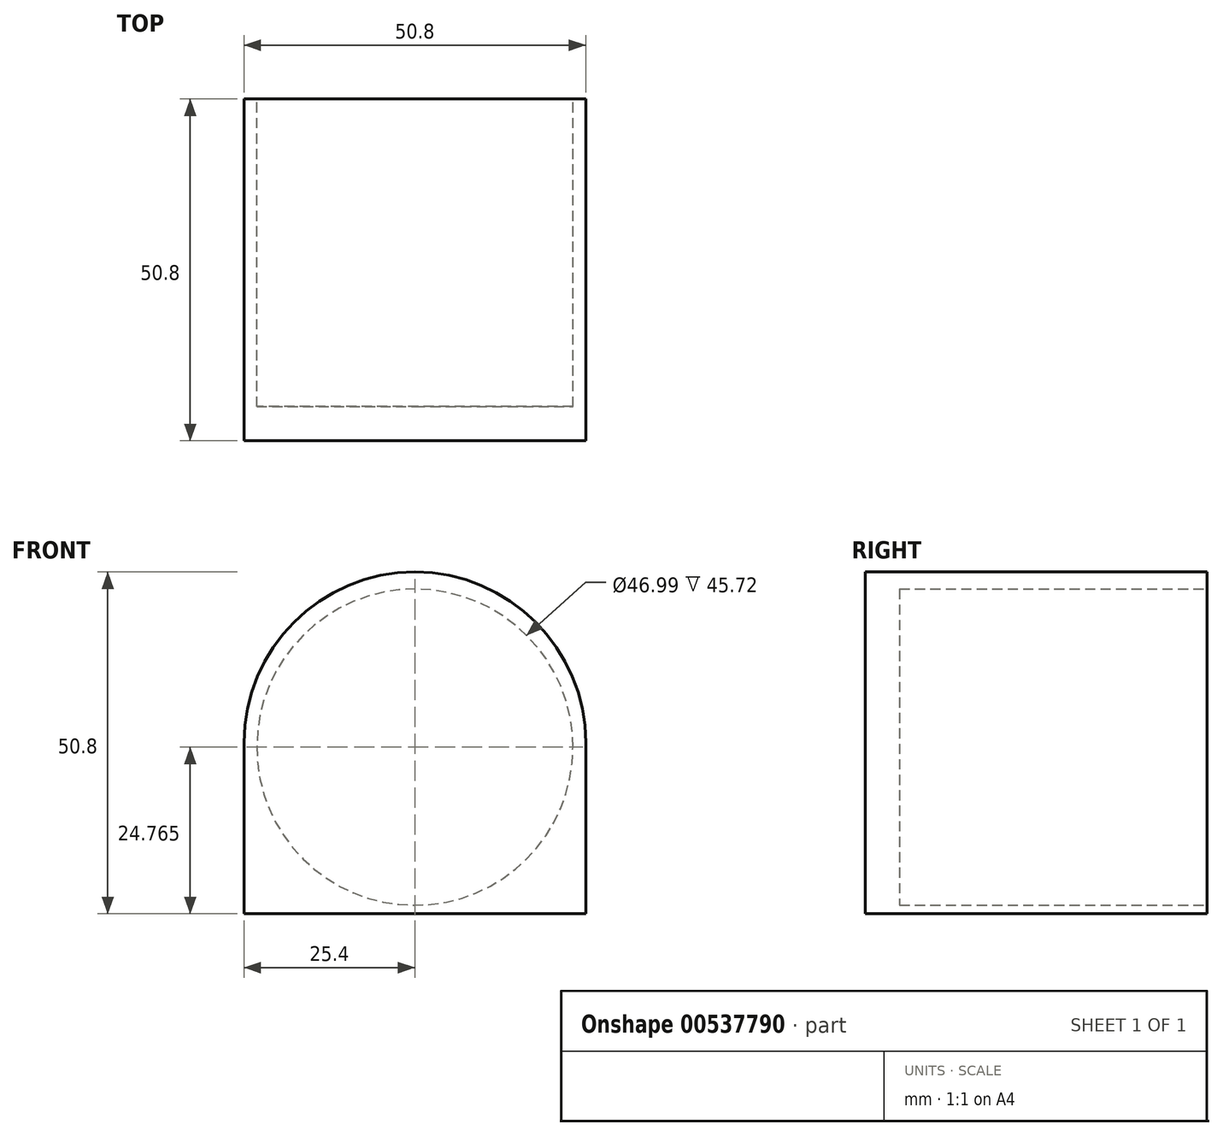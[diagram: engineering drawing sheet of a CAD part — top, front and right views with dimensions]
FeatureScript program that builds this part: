
annotation { "Feature Type Name" : "Feature", "Feature Type Description" : "" }
export const myFeature = defineFeature(function(context is Context, id is Id, definition is map)
    precondition{}
    {
        {
            var Q0;
            Q0=qCreatedBy(makeId("Top.planeOp"),FACE);
            var sketch = newSketch(context, id + "F0", { "sketchPlane" : qUnion([Q0])});
            skLineSegment(sketch, "E0", {"start": v(0, 0) * mm, "end": v(-50.8, 0) * mm});
            skLineSegment(sketch, "E1", {"start": v(-50.8, 0) * mm, "end": v(-50.8, 50.8) * mm});
            skLineSegment(sketch, "E2", {"start": v(-50.8, 50.8) * mm, "end": v(0, 50.8) * mm});
            skLineSegment(sketch, "E3", {"start": v(0, 50.8) * mm, "end": v(0, 0) * mm});
            skSolve(sketch);
        }
        {
            var Q0;
            Q0=makeQuery(id+"F0.imprint","IMPRINT",FACE,{"disambiguationData":[TD([[makeQuery(id+"F0.imprint","IMPRINT",EDGE,{"derivedFrom":sQuery(id+"F0.wireOp",EDGE,"E0")}),-1.0]])]});
            extrude(context, id + "F1", {"entities" : qUnion([Q0]), "depth" : 50.8 * mm, "offsetDistance" : 25.4 * mm});
        }
        {
            var Q0;
            Q0=makeQuery(id+"F1.opExtrude","SWEPT_FACE",FACE,{"disambiguationData":[OSD([sQuery(id+"F0.wireOp",EDGE,"E2")])]});
            var sketch = newSketch(context, id + "F2", { "sketchPlane" : qUnion([Q0])});
            skCircle(sketch, "E4", {"center": v(25.4, 24.77) * mm, "radius": 23.5 * mm});
            skSolve(sketch);
        }
        {
            var Q0;
            Q0=makeQuery(id+"F1.opExtrude","CAP_EDGE",EDGE,{"disambiguationData":[OSD([sQuery(id+"F0.wireOp",EDGE,"E3")])],"isStart":false});
            var Q1;
            Q1=makeQuery(id+"F1.opExtrude","CAP_EDGE",EDGE,{"disambiguationData":[OSD([sQuery(id+"F0.wireOp",EDGE,"E1")])],"isStart":false});
            fillet(context, id + "F3", {"entities" : qUnion([Q0, Q1]), "radius" : 25.4 * mm, "tangentPropagation" : true, "allowEdgeOverflow" : false});
        }
        {
            var Q0;
            Q0=makeQuery(id+"F2.imprint","IMPRINT",FACE,{"disambiguationData":[TD([[makeQuery(id+"F2.imprint","IMPRINT",EDGE,{"derivedFrom":sQuery(id+"F2.wireOp",EDGE,"E4")}),1.0]])]});
            extrude(context, id + "F4", {"entities" : qUnion([Q0]), "operationType" : NewBodyOperationType.REMOVE, "oppositeDirection" : true, "depth" : 45.72 * mm, "offsetDistance" : 25.4 * mm});
        }
    });
